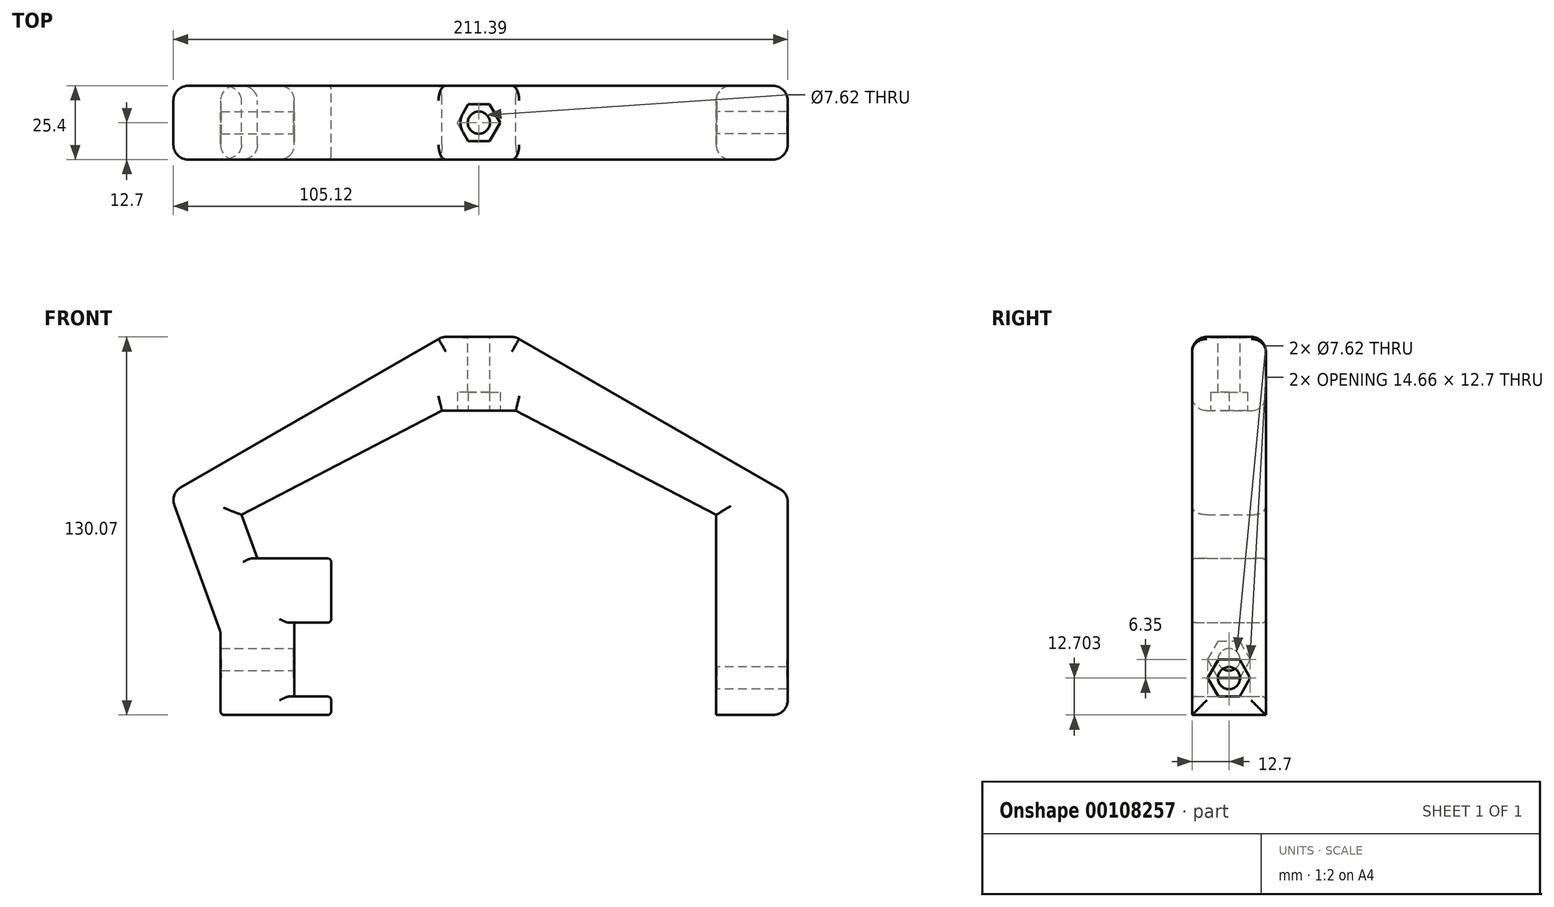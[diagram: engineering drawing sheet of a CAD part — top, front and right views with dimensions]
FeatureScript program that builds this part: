
annotation { "Feature Type Name" : "Feature", "Feature Type Description" : "" }
export const myFeature = defineFeature(function(context is Context, id is Id, definition is map)
    precondition{}
    {
        {
            assignVariable(context, id + "F0", {"name" : "NutDepth", "anyValue" : .25});
        }
        {
            var Q0;
            Q0=qCreatedBy(makeId("Front.planeOp"),FACE);
            var sketch = newSketch(context, id + "F1", { "sketchPlane" : qUnion([Q0])});
            skLineSegment(sketch, "E0", {"start": v(-63.5, 12.08) * mm, "end": v(-63.5, -13.32) * mm});
            skLineSegment(sketch, "E1", {"start": v(-63.5, -13.32) * mm, "end": v(-88.9, -13.32) * mm});
            skLineSegment(sketch, "E2", {"start": v(-63.5, 12.08) * mm, "end": v(-76.2, 12.08) * mm});
            skPoint(sketch, "E3", {"position": v(0, 62.88) * mm});
            skLineSegment(sketch, "E4", {"start": v(-88.9, -13.32) * mm, "end": v(-106.27, 34.41) * mm});
            skLineSegment(sketch, "E5", {"start": v(-76.2, 12.08) * mm, "end": v(-81.66, 27.07) * mm});
            skLineSegment(sketch, "E6", {"start": v(0, 62.88) * mm, "end": v(-12.7, 62.88) * mm});
            skLineSegment(sketch, "E7", {"start": v(0, 88.28) * mm, "end": v(-12.7, 88.28) * mm});
            skLineSegment(sketch, "E8", {"start": v(-81.66, 27.07) * mm, "end": v(-12.7, 62.88) * mm});
            skLineSegment(sketch, "E9", {"start": v(-106.27, 34.41) * mm, "end": v(-12.7, 88.28) * mm});
            skLineSegment(sketch, "E10.MirrorCS", {"start": v(0, 88.28) * mm, "end": v(12.7, 88.28) * mm});
            skLineSegment(sketch, "E11.MirrorCS", {"start": v(106.27, 34.41) * mm, "end": v(12.7, 88.28) * mm});
            skLineSegment(sketch, "E12.MirrorCS", {"start": v(0, 62.88) * mm, "end": v(12.7, 62.88) * mm});
            skLineSegment(sketch, "E13.MirrorCS", {"start": v(81.66, 27.07) * mm, "end": v(12.7, 62.88) * mm});
            skLineSegment(sketch, "E14", {"start": v(81.66, -41.79) * mm, "end": v(106.27, -41.79) * mm});
            skLineSegment(sketch, "E15", {"start": v(106.27, -41.79) * mm, "end": v(106.27, 34.41) * mm});
            skLineSegment(sketch, "E16", {"start": v(81.66, 27.07) * mm, "end": v(81.66, -41.79) * mm});
            skLineSegment(sketch, "E17", {"start": v(-106.27, 34.41) * mm, "end": v(-81.66, 27.07) * mm});
            skLineSegment(sketch, "E18", {"start": v(81.66, 27.07) * mm, "end": v(106.27, 34.41) * mm});
            skSolve(sketch);
        }
        {
            var Q0;
            Q0 = qSketchRegion(id + "F1", true);
            extrude(context, id + "F2", {"entities" : qUnion([Q0]), "endBound" : BoundingType.SYMMETRIC, "depth" : 25.4 * mm});
        }
        {
            var Q0;
            Q0=makeQuery(id+"F2.opExtrude","SWEPT_FACE",FACE,{"disambiguationData":[OSD([sQuery(id+"F1.wireOp",EDGE,"E1")])]});
            var Q1;
            Q1=makeQuery(id+"F2.opExtrude","SWEPT_FACE",FACE,{"disambiguationData":[OSD([sQuery(id+"F1.wireOp",EDGE,"E14")])]});
            extrude(context, id + "F3", {"entities" : qUnion([Q0]), "operationType" : NewBodyOperationType.ADD, "endBound" : BoundingType.UP_TO_SURFACE, "endBoundEntityFace" : qUnion([Q1]), "depth" : 25.4 * mm});
        }
        {
            var Q0;
            Q0=makeQuery(id+"F2.opExtrude","SWEPT_FACE",FACE,{"disambiguationData":[OSD([sQuery(id+"F1.wireOp",EDGE,"E16")])]});
            var sketch = newSketch(context, id + "F4", { "sketchPlane" : qUnion([Q0])});
            skLineSegment(sketch, "E19.0.1", {"start": v(-12.7, -41.79) * mm, "end": v(12.7, -41.79) * mm});
            skCircle(sketch, "E20", {"center": v(0, -29.09) * mm, "radius": 3.81 * mm});
            skCircle(sketch, "E21", {"center": v(0, -29.09) * mm, "radius": 6.35 * mm});
            skCircle(sketch, "E22.cCircle", {"center": v(0, -29.09) * mm, "radius": 6.35 * mm, "construction": true});
            skLineSegment(sketch, "E22.0", {"start": v(-3.67, -35.44) * mm, "end": v(-7.33, -29.09) * mm});
            skLineSegment(sketch, "E22.1", {"start": v(-7.33, -29.09) * mm, "end": v(-3.67, -22.74) * mm});
            skLineSegment(sketch, "E22.2", {"start": v(-3.67, -22.74) * mm, "end": v(3.67, -22.74) * mm});
            skLineSegment(sketch, "E22.3", {"start": v(3.67, -22.74) * mm, "end": v(7.33, -29.09) * mm});
            skLineSegment(sketch, "E22.4", {"start": v(7.33, -29.09) * mm, "end": v(3.67, -35.44) * mm});
            skLineSegment(sketch, "E22.5", {"start": v(3.67, -35.44) * mm, "end": v(-3.67, -35.44) * mm});
            skPoint(sketch, "E22.0.midPoint", {"position": v(-5.5, -32.26) * mm});
            skSolve(sketch);
        }
        {
            var Q0;
            {var subQ0=sQuery(id+"F4.wireOp",EDGE,"E22.2");var subQ1=sQuery(id+"F4.wireOp",EDGE,"E21");var subQ2=makeQuery(id+"F4.imprint","INTERSECT",VERTEX,{"derivedFrom":[subQ1,subQ0]});Q0=makeQuery(id+"F4.imprint","IMPRINT",FACE,{"disambiguationData":[TD([[makeQuery(id+"F4.imprint","IMPRINT",EDGE,{"disambiguationData":[TD([[subQ2,-1.0]])],"derivedFrom":subQ1}),-1.0]])]});}
            var Q1;
            Q1=makeQuery(id+"F4.imprint","IMPRINT",FACE,{"disambiguationData":[TD([[makeQuery(id+"F4.imprint","IMPRINT",EDGE,{"derivedFrom":sQuery(id+"F4.wireOp",EDGE,"E20")}),-1.0]])]});
            var Q2;
            {var subQ0=sQuery(id+"F4.wireOp",EDGE,"E22.1");var subQ1=sQuery(id+"F4.wireOp",EDGE,"E21");var subQ2=makeQuery(id+"F4.imprint","INTERSECT",VERTEX,{"derivedFrom":[subQ1,subQ0]});Q2=makeQuery(id+"F4.imprint","IMPRINT",FACE,{"disambiguationData":[TD([[makeQuery(id+"F4.imprint","IMPRINT",EDGE,{"disambiguationData":[TD([[subQ2,-1.0]])],"derivedFrom":subQ1}),-1.0]])]});}
            var Q3;
            {var subQ0=sQuery(id+"F4.wireOp",EDGE,"E22.2");var subQ1=sQuery(id+"F4.wireOp",EDGE,"E21");var subQ2=makeQuery(id+"F4.imprint","INTERSECT",VERTEX,{"derivedFrom":[subQ1,subQ0]});Q3=makeQuery(id+"F4.imprint","IMPRINT",FACE,{"disambiguationData":[TD([[makeQuery(id+"F4.imprint","IMPRINT",EDGE,{"disambiguationData":[TD([[subQ2,1.0]])],"derivedFrom":subQ1}),-1.0]])]});}
            var Q4;
            {var subQ0=sQuery(id+"F4.wireOp",EDGE,"E22.3");var subQ1=sQuery(id+"F4.wireOp",EDGE,"E21");var subQ2=makeQuery(id+"F4.imprint","INTERSECT",VERTEX,{"derivedFrom":[subQ1,subQ0]});Q4=makeQuery(id+"F4.imprint","IMPRINT",FACE,{"disambiguationData":[TD([[makeQuery(id+"F4.imprint","IMPRINT",EDGE,{"disambiguationData":[TD([[subQ2,1.0]])],"derivedFrom":subQ1}),-1.0]])]});}
            var Q5;
            {var subQ0=sQuery(id+"F4.wireOp",EDGE,"E22.5");var subQ1=sQuery(id+"F4.wireOp",EDGE,"E21");var subQ2=makeQuery(id+"F4.imprint","INTERSECT",VERTEX,{"derivedFrom":[subQ1,subQ0]});Q5=makeQuery(id+"F4.imprint","IMPRINT",FACE,{"disambiguationData":[TD([[makeQuery(id+"F4.imprint","IMPRINT",EDGE,{"disambiguationData":[TD([[subQ2,-1.0]])],"derivedFrom":subQ1}),-1.0]])]});}
            var Q6;
            {var subQ0=sQuery(id+"F4.wireOp",EDGE,"E22.0");var subQ1=sQuery(id+"F4.wireOp",EDGE,"E21");var subQ2=makeQuery(id+"F4.imprint","INTERSECT",VERTEX,{"derivedFrom":[subQ1,subQ0]});Q6=makeQuery(id+"F4.imprint","IMPRINT",FACE,{"disambiguationData":[TD([[makeQuery(id+"F4.imprint","IMPRINT",EDGE,{"disambiguationData":[TD([[subQ2,-1.0]])],"derivedFrom":subQ1}),-1.0]])]});}
            extrude(context, id + "F5", {"entities" : qUnion([Q0, Q1, Q2, Q3, Q4, Q5, Q6]), "operationType" : NewBodyOperationType.REMOVE, "oppositeDirection" : true, "depth" : (getVariable(context, 'NutDepth')) * mm});
        }
        {
            var Q0;
            Q0=makeQuery(id+"F5.boolean.opBoolean","SPLIT",FACE,{"disambiguationData":[TD([makeQuery(id+"F5.opExtrude","SWEPT_FACE",FACE,{"disambiguationData":[OSD([sQuery(id+"F4.wireOp",EDGE,"E20")])]})])],"derivedFrom":makeQuery(id+"F2.opExtrude","SWEPT_FACE",FACE,{"disambiguationData":[OSD([sQuery(id+"F1.wireOp",EDGE,"E16")])]})});
            extrude(context, id + "F6", {"entities" : qUnion([Q0]), "operationType" : NewBodyOperationType.REMOVE, "endBound" : BoundingType.THROUGH_ALL, "oppositeDirection" : true, "depth" : 25.4 * mm});
        }
        {
            var Q0;
            Q0=makeQuery(id+"F2.opExtrude","SWEPT_FACE",FACE,{"disambiguationData":[OSD([sQuery(id+"F1.wireOp",EDGE,"E15")])]});
            var sketch = newSketch(context, id + "F7", { "sketchPlane" : qUnion([Q0])});
            skLineSegment(sketch, "E23.0", {"start": v(3.67, -22.74) * mm, "end": v(-3.67, -22.74) * mm});
            skLineSegment(sketch, "E24.0", {"start": v(-3.67, -22.74) * mm, "end": v(-7.33, -29.09) * mm});
            skLineSegment(sketch, "E25.0", {"start": v(-7.33, -29.09) * mm, "end": v(-3.67, -35.44) * mm});
            skLineSegment(sketch, "E26.0", {"start": v(-3.67, -35.44) * mm, "end": v(3.67, -35.44) * mm});
            skLineSegment(sketch, "E27.0", {"start": v(3.67, -35.44) * mm, "end": v(7.33, -29.09) * mm});
            skLineSegment(sketch, "E28.0", {"start": v(7.33, -29.09) * mm, "end": v(3.67, -22.74) * mm});
            skSolve(sketch);
        }
        {
            var Q0;
            Q0=makeQuery(id+"F7.imprint","IMPRINT",FACE,{"disambiguationData":[TD([[makeQuery(id+"F7.imprint","IMPRINT",EDGE,{"derivedFrom":sQuery(id+"F7.wireOp",EDGE,"E23.0")}),1.0]])]});
            extrude(context, id + "F8", {"entities" : qUnion([Q0]), "operationType" : NewBodyOperationType.REMOVE, "oppositeDirection" : true, "depth" : (getVariable(context, 'NutDepth')) * mm});
        }
        {
            var Q0;
            Q0=makeQuery(id+"F2.opExtrude","SWEPT_FACE",FACE,{"disambiguationData":[OSD([sQuery(id+"F1.wireOp",EDGE,"E7"),sQuery(id+"F1.wireOp",EDGE,"E10.MirrorCS")])]});
            var sketch = newSketch(context, id + "F9", { "sketchPlane" : qUnion([Q0])});
            skLineSegment(sketch, "E29.0.0", {"start": v(12.7, 12.7) * mm, "end": v(-12.7, 12.7) * mm});
            skLineSegment(sketch, "E29.0.1", {"start": v(-12.7, 12.7) * mm, "end": v(-12.7, -12.7) * mm});
            skLineSegment(sketch, "E29.0.2", {"start": v(-12.7, -12.7) * mm, "end": v(12.7, -12.7) * mm});
            skLineSegment(sketch, "E29.0.3", {"start": v(12.7, -12.7) * mm, "end": v(12.7, 12.7) * mm});
            skCircle(sketch, "E30", {"center": v(0, 0) * mm, "radius": 3.81 * mm});
            skCircle(sketch, "E31", {"center": v(0, 0) * mm, "radius": 6.35 * mm});
            skCircle(sketch, "E32.cCircle", {"center": v(0, 0) * mm, "radius": 6.35 * mm, "construction": true});
            skLineSegment(sketch, "E32.0", {"start": v(7.33, 0) * mm, "end": v(3.67, -6.35) * mm});
            skLineSegment(sketch, "E32.1", {"start": v(3.67, -6.35) * mm, "end": v(-3.67, -6.35) * mm});
            skLineSegment(sketch, "E32.2", {"start": v(-3.67, -6.35) * mm, "end": v(-7.33, 0) * mm});
            skLineSegment(sketch, "E32.3", {"start": v(-7.33, 0) * mm, "end": v(-3.67, 6.35) * mm});
            skLineSegment(sketch, "E32.4", {"start": v(-3.67, 6.35) * mm, "end": v(3.67, 6.35) * mm});
            skLineSegment(sketch, "E32.5", {"start": v(3.67, 6.35) * mm, "end": v(7.33, 0) * mm});
            skPoint(sketch, "E32.0.midPoint", {"position": v(5.5, -3.18) * mm});
            skSolve(sketch);
        }
        {
            var Q0;
            {var subQ0=sQuery(id+"F9.wireOp",EDGE,"E32.4");var subQ1=sQuery(id+"F9.wireOp",EDGE,"E31");var subQ2=makeQuery(id+"F9.imprint","INTERSECT",VERTEX,{"derivedFrom":[subQ1,subQ0]});Q0=makeQuery(id+"F9.imprint","IMPRINT",FACE,{"disambiguationData":[TD([[makeQuery(id+"F9.imprint","IMPRINT",EDGE,{"disambiguationData":[TD([[subQ2,-1.0]])],"derivedFrom":subQ1}),-1.0]])]});}
            var Q1;
            {var subQ0=sQuery(id+"F9.wireOp",EDGE,"E32.4");var subQ1=sQuery(id+"F9.wireOp",EDGE,"E31");var subQ2=makeQuery(id+"F9.imprint","INTERSECT",VERTEX,{"derivedFrom":[subQ1,subQ0]});Q1=makeQuery(id+"F9.imprint","IMPRINT",FACE,{"disambiguationData":[TD([[makeQuery(id+"F9.imprint","IMPRINT",EDGE,{"disambiguationData":[TD([[subQ2,1.0]])],"derivedFrom":subQ1}),-1.0]])]});}
            var Q2;
            {var subQ0=sQuery(id+"F9.wireOp",EDGE,"E32.5");var subQ1=sQuery(id+"F9.wireOp",EDGE,"E31");var subQ2=makeQuery(id+"F9.imprint","INTERSECT",VERTEX,{"derivedFrom":[subQ1,subQ0]});Q2=makeQuery(id+"F9.imprint","IMPRINT",FACE,{"disambiguationData":[TD([[makeQuery(id+"F9.imprint","IMPRINT",EDGE,{"disambiguationData":[TD([[subQ2,1.0]])],"derivedFrom":subQ1}),-1.0]])]});}
            var Q3;
            {var subQ0=sQuery(id+"F9.wireOp",EDGE,"E32.1");var subQ1=sQuery(id+"F9.wireOp",EDGE,"E31");var subQ2=makeQuery(id+"F9.imprint","INTERSECT",VERTEX,{"derivedFrom":[subQ1,subQ0]});Q3=makeQuery(id+"F9.imprint","IMPRINT",FACE,{"disambiguationData":[TD([[makeQuery(id+"F9.imprint","IMPRINT",EDGE,{"disambiguationData":[TD([[subQ2,-1.0]])],"derivedFrom":subQ1}),-1.0]])]});}
            var Q4;
            {var subQ0=sQuery(id+"F9.wireOp",EDGE,"E32.2");var subQ1=sQuery(id+"F9.wireOp",EDGE,"E31");var subQ2=makeQuery(id+"F9.imprint","INTERSECT",VERTEX,{"derivedFrom":[subQ1,subQ0]});Q4=makeQuery(id+"F9.imprint","IMPRINT",FACE,{"disambiguationData":[TD([[makeQuery(id+"F9.imprint","IMPRINT",EDGE,{"disambiguationData":[TD([[subQ2,-1.0]])],"derivedFrom":subQ1}),-1.0]])]});}
            var Q5;
            Q5=makeQuery(id+"F9.imprint","IMPRINT",FACE,{"disambiguationData":[TD([[makeQuery(id+"F9.imprint","IMPRINT",EDGE,{"derivedFrom":sQuery(id+"F9.wireOp",EDGE,"E30")}),-1.0]])]});
            extrude(context, id + "F10", {"entities" : qUnion([Q0, Q1, Q2, Q3, Q4, Q5]), "operationType" : NewBodyOperationType.REMOVE, "oppositeDirection" : true, "depth" : (getVariable(context, 'NutDepth')) * mm});
        }
        {
            var Q0;
            Q0=makeQuery(id+"F9.imprint","IMPRINT",FACE,{"disambiguationData":[TD([[makeQuery(id+"F9.imprint","IMPRINT",EDGE,{"derivedFrom":sQuery(id+"F9.wireOp",EDGE,"E30")}),1.0]])]});
            extrude(context, id + "F11", {"entities" : qUnion([Q0]), "operationType" : NewBodyOperationType.REMOVE, "endBound" : BoundingType.THROUGH_ALL, "oppositeDirection" : true, "depth" : 25.4 * mm});
        }
        {
            var Q0;
            Q0=makeQuery(id+"F2.opExtrude","SWEPT_FACE",FACE,{"disambiguationData":[OSD([sQuery(id+"F1.wireOp",EDGE,"E6"),sQuery(id+"F1.wireOp",EDGE,"E12.MirrorCS")])]});
            var sketch = newSketch(context, id + "F12", { "sketchPlane" : qUnion([Q0])});
            skLineSegment(sketch, "E33.0", {"start": v(-3.67, 6.35) * mm, "end": v(-7.33, 0) * mm});
            skLineSegment(sketch, "E34.0", {"start": v(-7.33, 0) * mm, "end": v(-3.67, -6.35) * mm});
            skLineSegment(sketch, "E35.0", {"start": v(-3.67, -6.35) * mm, "end": v(3.67, -6.35) * mm});
            skLineSegment(sketch, "E36.0", {"start": v(3.67, -6.35) * mm, "end": v(7.33, 0) * mm});
            skLineSegment(sketch, "E37.0", {"start": v(7.33, 0) * mm, "end": v(3.67, 6.35) * mm});
            skLineSegment(sketch, "E38.0", {"start": v(3.67, 6.35) * mm, "end": v(-3.67, 6.35) * mm});
            skSolve(sketch);
        }
        {
            var Q0;
            Q0=makeQuery(id+"F12.imprint","IMPRINT",FACE,{"disambiguationData":[TD([[makeQuery(id+"F12.imprint","IMPRINT",EDGE,{"derivedFrom":sQuery(id+"F12.wireOp",EDGE,"E33.0")}),1.0]])]});
            extrude(context, id + "F13", {"entities" : qUnion([Q0]), "operationType" : NewBodyOperationType.REMOVE, "oppositeDirection" : true, "depth" : 6.35 * mm});
        }
        {
            var Q0;
            {var subQ0=sQuery(id+"F1.wireOp",EDGE,"E0");Q0=makeQuery(id+"F3.boolean.opBoolean","MERGE",FACE,{"derivedFrom":[makeQuery(id+"F2.opExtrude","SWEPT_FACE",FACE,{"disambiguationData":[OSD([subQ0])]}),makeQuery(id+"F3.opExtrude","SWEPT_FACE",FACE,{"disambiguationData":[OSD([subQ0,sQuery(id+"F1.wireOp",EDGE,"E1")])]})]});}
            var sketch = newSketch(context, id + "F14", { "sketchPlane" : qUnion([Q0])});
            skLineSegment(sketch, "E39.0.3", {"start": v(-12.7, -41.79) * mm, "end": v(12.7, -41.79) * mm});
            skLineSegment(sketch, "E40.0", {"start": v(-12.7, -16.39) * mm, "end": v(12.7, -16.39) * mm});
            skPoint(sketch, "E41.center.orphan", {"position": v(0, -22.74) * mm});
            skCircle(sketch, "E42", {"center": v(0, -22.74) * mm, "radius": 3.81 * mm});
            skCircle(sketch, "E43", {"center": v(0, -22.74) * mm, "radius": 6.35 * mm});
            skCircle(sketch, "E44.cCircle", {"center": v(0, -22.74) * mm, "radius": 6.35 * mm, "construction": true});
            skLineSegment(sketch, "E44.0", {"start": v(7.33, -22.74) * mm, "end": v(3.67, -29.09) * mm});
            skLineSegment(sketch, "E44.1", {"start": v(3.67, -29.09) * mm, "end": v(-3.67, -29.09) * mm});
            skLineSegment(sketch, "E44.2", {"start": v(-3.67, -29.09) * mm, "end": v(-7.33, -22.74) * mm});
            skLineSegment(sketch, "E44.3", {"start": v(-7.33, -22.74) * mm, "end": v(-3.67, -16.39) * mm});
            skLineSegment(sketch, "E44.4", {"start": v(-3.67, -16.39) * mm, "end": v(3.67, -16.39) * mm});
            skLineSegment(sketch, "E44.5", {"start": v(3.67, -16.39) * mm, "end": v(7.33, -22.74) * mm});
            skPoint(sketch, "E44.0.midPoint", {"position": v(5.5, -25.91) * mm});
            skLineSegment(sketch, "E45.0", {"start": v(-12.7, -10.04) * mm, "end": v(12.7, -10.04) * mm});
            skLineSegment(sketch, "E46.0", {"start": v(-12.7, -35.44) * mm, "end": v(12.7, -35.44) * mm});
            skSolve(sketch);
        }
        {
            var Q0;
            Q0=makeQuery(id+"F14.imprint","IMPRINT",FACE,{"disambiguationData":[TD([[makeQuery(id+"F14.imprint","IMPRINT",EDGE,{"derivedFrom":sQuery(id+"F14.wireOp",EDGE,"E42")}),-1.0]])]});
            var Q1;
            {var subQ0=sQuery(id+"F14.wireOp",EDGE,"E44.4");var subQ1=sQuery(id+"F14.wireOp",EDGE,"E43");var subQ2=makeQuery(id+"F14.imprint","INTERSECT",VERTEX,{"derivedFrom":[subQ1,subQ0]});Q1=makeQuery(id+"F14.imprint","IMPRINT",FACE,{"disambiguationData":[TD([[makeQuery(id+"F14.imprint","IMPRINT",EDGE,{"disambiguationData":[TD([[subQ2,-1.0]])],"derivedFrom":subQ1}),-1.0]])]});}
            var Q2;
            {var subQ0=sQuery(id+"F14.wireOp",EDGE,"E44.3");var subQ1=sQuery(id+"F14.wireOp",EDGE,"E43");var subQ2=makeQuery(id+"F14.imprint","INTERSECT",VERTEX,{"derivedFrom":[subQ1,subQ0]});Q2=makeQuery(id+"F14.imprint","IMPRINT",FACE,{"disambiguationData":[TD([[makeQuery(id+"F14.imprint","IMPRINT",EDGE,{"disambiguationData":[TD([[subQ2,-1.0]])],"derivedFrom":subQ1}),-1.0]])]});}
            var Q3;
            {var subQ0=sQuery(id+"F14.wireOp",EDGE,"E44.2");var subQ1=sQuery(id+"F14.wireOp",EDGE,"E43");var subQ2=makeQuery(id+"F14.imprint","INTERSECT",VERTEX,{"derivedFrom":[subQ1,subQ0]});Q3=makeQuery(id+"F14.imprint","IMPRINT",FACE,{"disambiguationData":[TD([[makeQuery(id+"F14.imprint","IMPRINT",EDGE,{"disambiguationData":[TD([[subQ2,-1.0]])],"derivedFrom":subQ1}),-1.0]])]});}
            var Q4;
            {var subQ0=sQuery(id+"F14.wireOp",EDGE,"E44.1");var subQ1=sQuery(id+"F14.wireOp",EDGE,"E43");var subQ2=makeQuery(id+"F14.imprint","INTERSECT",VERTEX,{"derivedFrom":[subQ1,subQ0]});Q4=makeQuery(id+"F14.imprint","IMPRINT",FACE,{"disambiguationData":[TD([[makeQuery(id+"F14.imprint","IMPRINT",EDGE,{"disambiguationData":[TD([[subQ2,-1.0]])],"derivedFrom":subQ1}),-1.0]])]});}
            var Q5;
            {var subQ0=sQuery(id+"F14.wireOp",EDGE,"E44.5");var subQ1=sQuery(id+"F14.wireOp",EDGE,"E43");var subQ2=makeQuery(id+"F14.imprint","INTERSECT",VERTEX,{"derivedFrom":[subQ1,subQ0]});Q5=makeQuery(id+"F14.imprint","IMPRINT",FACE,{"disambiguationData":[TD([[makeQuery(id+"F14.imprint","IMPRINT",EDGE,{"disambiguationData":[TD([[subQ2,1.0]])],"derivedFrom":subQ1}),-1.0]])]});}
            var Q6;
            {var subQ0=sQuery(id+"F14.wireOp",EDGE,"E44.4");var subQ1=sQuery(id+"F14.wireOp",EDGE,"E43");var subQ2=makeQuery(id+"F14.imprint","INTERSECT",VERTEX,{"derivedFrom":[subQ1,subQ0]});Q6=makeQuery(id+"F14.imprint","IMPRINT",FACE,{"disambiguationData":[TD([[makeQuery(id+"F14.imprint","IMPRINT",EDGE,{"disambiguationData":[TD([[subQ2,1.0]])],"derivedFrom":subQ1}),-1.0]])]});}
            extrude(context, id + "F15", {"entities" : qUnion([Q0, Q1, Q2, Q3, Q4, Q5, Q6]), "operationType" : NewBodyOperationType.REMOVE, "oppositeDirection" : true, "depth" : (getVariable(context, 'NutDepth')) * mm});
        }
        {
            var Q0;
            Q0=makeQuery(id+"F14.imprint","IMPRINT",FACE,{"disambiguationData":[TD([[makeQuery(id+"F14.imprint","IMPRINT",EDGE,{"derivedFrom":sQuery(id+"F14.wireOp",EDGE,"E42")}),1.0]])]});
            extrude(context, id + "F16", {"entities" : qUnion([Q0]), "operationType" : NewBodyOperationType.REMOVE, "endBound" : BoundingType.THROUGH_ALL, "oppositeDirection" : true, "depth" : 25.4 * mm});
        }
        {
            var Q0;
            Q0=makeQuery(id+"F3.opExtrude","SWEPT_FACE",FACE,{"disambiguationData":[OSD([sQuery(id+"F1.wireOp",EDGE,"E1"),sQuery(id+"F1.wireOp",EDGE,"E4")])]});
            var sketch = newSketch(context, id + "F17", { "sketchPlane" : qUnion([Q0])});
            skLineSegment(sketch, "E47.0", {"start": v(3.67, -16.39) * mm, "end": v(-3.67, -16.39) * mm});
            skLineSegment(sketch, "E48.0", {"start": v(-3.67, -16.39) * mm, "end": v(-7.33, -22.74) * mm});
            skLineSegment(sketch, "E49.0", {"start": v(-7.33, -22.74) * mm, "end": v(-3.67, -29.09) * mm});
            skLineSegment(sketch, "E50.0", {"start": v(-3.67, -29.09) * mm, "end": v(3.67, -29.09) * mm});
            skLineSegment(sketch, "E51.0", {"start": v(3.67, -29.09) * mm, "end": v(7.33, -22.74) * mm});
            skLineSegment(sketch, "E52.0", {"start": v(7.33, -22.74) * mm, "end": v(3.67, -16.39) * mm});
            skSolve(sketch);
        }
        {
            var Q0;
            Q0=makeQuery(id+"F17.imprint","IMPRINT",FACE,{"disambiguationData":[TD([[makeQuery(id+"F17.imprint","IMPRINT",EDGE,{"derivedFrom":sQuery(id+"F17.wireOp",EDGE,"E47.0")}),1.0]])]});
            extrude(context, id + "F18", {"entities" : qUnion([Q0]), "operationType" : NewBodyOperationType.REMOVE, "oppositeDirection" : true, "depth" : (getVariable(context, 'NutDepth')) * mm});
        }
        {
            var Q0;
            Q0=makeQuery(id+"F2.opExtrude","CAP_EDGE",EDGE,{"disambiguationData":[OSD([sQuery(id+"F1.wireOp",EDGE,"E9")])],"isStart":false});
            var Q1;
            Q1=makeQuery(id+"F2.opExtrude","CAP_EDGE",EDGE,{"disambiguationData":[OSD([sQuery(id+"F1.wireOp",EDGE,"E11.MirrorCS")])],"isStart":false});
            var Q2;
            Q2=makeQuery(id+"F2.opExtrude","CAP_EDGE",EDGE,{"disambiguationData":[OSD([sQuery(id+"F1.wireOp",EDGE,"E11.MirrorCS")])],"isStart":true});
            var Q3;
            Q3=makeQuery(id+"F2.opExtrude","CAP_EDGE",EDGE,{"disambiguationData":[OSD([sQuery(id+"F1.wireOp",EDGE,"E9")])],"isStart":true});
            var Q4;
            Q4=makeQuery(id+"F2.opExtrude","CAP_EDGE",EDGE,{"disambiguationData":[OSD([sQuery(id+"F1.wireOp",EDGE,"E15")])],"isStart":false});
            var Q5;
            Q5=makeQuery(id+"F2.opExtrude","CAP_EDGE",EDGE,{"disambiguationData":[OSD([sQuery(id+"F1.wireOp",EDGE,"E15")])],"isStart":true});
            var Q6;
            Q6=makeQuery(id+"F2.opExtrude","SWEPT_EDGE",EDGE,{"disambiguationData":[OSD([sQuery(id+"F1.wireOp",EDGE,"E11.MirrorCS"),sQuery(id+"F1.wireOp",EDGE,"E15"),sQuery(id+"F1.wireOp",EDGE,"E18")])]});
            var Q7;
            Q7=makeQuery(id+"F2.opExtrude","CAP_EDGE",EDGE,{"disambiguationData":[OSD([sQuery(id+"F1.wireOp",EDGE,"E16")])],"isStart":false});
            var Q8;
            Q8=makeQuery(id+"F2.opExtrude","CAP_EDGE",EDGE,{"disambiguationData":[OSD([sQuery(id+"F1.wireOp",EDGE,"E16")])],"isStart":true});
            var Q9;
            Q9=makeQuery(id+"F2.opExtrude","CAP_EDGE",EDGE,{"disambiguationData":[OSD([sQuery(id+"F1.wireOp",EDGE,"E13.MirrorCS")])],"isStart":true});
            var Q10;
            Q10=makeQuery(id+"F2.opExtrude","CAP_EDGE",EDGE,{"disambiguationData":[OSD([sQuery(id+"F1.wireOp",EDGE,"E13.MirrorCS")])],"isStart":false});
            var Q11;
            Q11=makeQuery(id+"F2.opExtrude","CAP_EDGE",EDGE,{"disambiguationData":[OSD([sQuery(id+"F1.wireOp",EDGE,"E6"),sQuery(id+"F1.wireOp",EDGE,"E12.MirrorCS")])],"isStart":true});
            var Q12;
            Q12=makeQuery(id+"F2.opExtrude","CAP_EDGE",EDGE,{"disambiguationData":[OSD([sQuery(id+"F1.wireOp",EDGE,"E6"),sQuery(id+"F1.wireOp",EDGE,"E12.MirrorCS")])],"isStart":false});
            var Q13;
            Q13=makeQuery(id+"F2.opExtrude","CAP_EDGE",EDGE,{"disambiguationData":[OSD([sQuery(id+"F1.wireOp",EDGE,"E8")])],"isStart":false});
            var Q14;
            Q14=makeQuery(id+"F2.opExtrude","CAP_EDGE",EDGE,{"disambiguationData":[OSD([sQuery(id+"F1.wireOp",EDGE,"E8")])],"isStart":true});
            var Q15;
            Q15=makeQuery(id+"F2.opExtrude","CAP_EDGE",EDGE,{"disambiguationData":[OSD([sQuery(id+"F1.wireOp",EDGE,"E5")])],"isStart":true});
            var Q16;
            Q16=makeQuery(id+"F2.opExtrude","CAP_EDGE",EDGE,{"disambiguationData":[OSD([sQuery(id+"F1.wireOp",EDGE,"E5")])],"isStart":false});
            var Q17;
            Q17=makeQuery(id+"F2.opExtrude","CAP_EDGE",EDGE,{"disambiguationData":[OSD([sQuery(id+"F1.wireOp",EDGE,"E4")])],"isStart":true});
            var Q18;
            Q18=makeQuery(id+"F2.opExtrude","CAP_EDGE",EDGE,{"disambiguationData":[OSD([sQuery(id+"F1.wireOp",EDGE,"E4")])],"isStart":false});
            var Q19;
            {var subQ0=sQuery(id+"F1.wireOp",EDGE,"E4");var subQ1=sQuery(id+"F1.wireOp",EDGE,"E1");Q19=makeQuery(id+"F3.opExtrude","SWEPT_EDGE",EDGE,{"disambiguationData":[OSD([subQ1,subQ0]),TDD([makeQuery(id+"F2.opExtrude","CAP_VERTEX",VERTEX,{"disambiguationData":[OSD([subQ1,subQ0])],"isStart":false})])]});}
            var Q20;
            {var subQ0=sQuery(id+"F1.wireOp",EDGE,"E4");var subQ1=sQuery(id+"F1.wireOp",EDGE,"E1");Q20=makeQuery(id+"F3.opExtrude","SWEPT_EDGE",EDGE,{"disambiguationData":[OSD([subQ1,subQ0]),TDD([makeQuery(id+"F2.opExtrude","CAP_VERTEX",VERTEX,{"disambiguationData":[OSD([subQ1,subQ0])],"isStart":true})])]});}
            var Q21;
            Q21=makeQuery(id+"F2.opExtrude","SWEPT_EDGE",EDGE,{"disambiguationData":[OSD([sQuery(id+"F1.wireOp",EDGE,"E4"),sQuery(id+"F1.wireOp",EDGE,"E9"),sQuery(id+"F1.wireOp",EDGE,"E17")])]});
            var Q22;
            {var subQ0=sQuery(id+"F1.wireOp",EDGE,"E4");var subQ1=sQuery(id+"F1.wireOp",EDGE,"E1");Q22=makeQuery(id+"F3.boolean.opBoolean","MERGE",EDGE,{"derivedFrom":[makeQuery(id+"F2.opExtrude","SWEPT_EDGE",EDGE,{"disambiguationData":[OSD([subQ1,subQ0])]}),makeQuery(id+"F3.opExtrude","CAP_EDGE",EDGE,{"disambiguationData":[OSD([subQ1,subQ0])],"isStart":true})]});}
            var Q23;
            Q23=makeQuery(id+"F3.opExtrude","TWEAK_EDGE",EDGE,{"derivedFrom":[makeQuery(id+"F2.opExtrude","SWEPT_EDGE",EDGE,{"disambiguationData":[OSD([sQuery(id+"F1.wireOp",EDGE,"E1"),sQuery(id+"F1.wireOp",EDGE,"E4")])]}),makeQuery(id+"F2.opExtrude","SWEPT_FACE",FACE,{"disambiguationData":[OSD([sQuery(id+"F1.wireOp",EDGE,"E14")])]})]});
            var Q24;
            Q24=makeQuery(id+"F2.opExtrude","SWEPT_EDGE",EDGE,{"disambiguationData":[OSD([sQuery(id+"F1.wireOp",EDGE,"E14"),sQuery(id+"F1.wireOp",EDGE,"E15")])]});
            fillet(context, id + "F19", {"entities" : qUnion([Q0, Q1, Q2, Q3, Q4, Q5, Q6, Q7, Q8, Q9, Q10, Q11, Q12, Q13, Q14, Q15, Q16, Q17, Q18, Q19, Q20, Q21, Q22, Q23, Q24]), "radius" : 5.08 * mm, "tangentPropagation" : true, "allowEdgeOverflow" : false});
        }
        {
            var Q0;
            Q0=makeQuery(id+"F2.opExtrude","CAP_EDGE",EDGE,{"disambiguationData":[OSD([sQuery(id+"F1.wireOp",EDGE,"E7"),sQuery(id+"F1.wireOp",EDGE,"E10.MirrorCS")])],"isStart":true});
            fillet(context, id + "F20", {"entities" : qUnion([Q0]), "radius" : 5.08 * mm, "tangentPropagation" : true, "allowEdgeOverflow" : false});
        }
        {
            var Q0;
            {var subQ0=sQuery(id+"F14.wireOp",EDGE,"E45.0");Q0=makeQuery(id+"F14.imprint","IMPRINT",FACE,{"disambiguationData":[TD([[makeQuery(id+"F14.imprint","IMPRINT",EDGE,{"derivedFrom":subQ0}),1.0]])]});}
            extrude(context, id + "F21", {"entities" : qUnion([Q0]), "operationType" : NewBodyOperationType.ADD, "depth" : 12.7 * mm});
        }
        {
            var Q0;
            {var subQ0=sQuery(id+"F14.wireOp",EDGE,"E39.0.3");Q0=makeQuery(id+"F14.imprint","IMPRINT",FACE,{"disambiguationData":[TD([[makeQuery(id+"F14.imprint","IMPRINT",EDGE,{"derivedFrom":subQ0}),-1.0]])]});}
            var Q1;
            Q1=makeQuery(id+"F21.opExtrude","CAP_FACE",FACE,{"disambiguationData":[OSD([sQuery(id+"F1.wireOp",EDGE,"E0"),sQuery(id+"F1.wireOp",EDGE,"E1"),sQuery(id+"F1.wireOp",EDGE,"E2"),sQuery(id+"F14.wireOp",EDGE,"E45.0")])],"isStart":false});
            extrude(context, id + "F22", {"entities" : qUnion([Q0]), "operationType" : NewBodyOperationType.ADD, "endBound" : BoundingType.UP_TO_SURFACE, "endBoundEntityFace" : qUnion([Q1]), "depth" : 25.4 * mm});
        }
        {
            var Q0;
            {var subQ0=sQuery(id+"F1.wireOp",EDGE,"E1");var subQ1=sQuery(id+"F1.wireOp",EDGE,"E0");Q0=makeQuery(id+"F3.boolean.opBoolean","MERGE",EDGE,{"derivedFrom":[makeQuery(id+"F2.opExtrude","CAP_EDGE",EDGE,{"disambiguationData":[OSD([subQ1])],"isStart":false}),makeQuery(id+"F3.opExtrude","SWEPT_EDGE",EDGE,{"disambiguationData":[OSD([subQ1,subQ0]),TDD([makeQuery(id+"F2.opExtrude","CAP_VERTEX",VERTEX,{"disambiguationData":[OSD([subQ1,subQ0])],"isStart":false})])]})]});}
            var Q1;
            {var subQ0=sQuery(id+"F1.wireOp",EDGE,"E1");var subQ1=sQuery(id+"F1.wireOp",EDGE,"E0");Q1=makeQuery(id+"F3.boolean.opBoolean","MERGE",EDGE,{"derivedFrom":[makeQuery(id+"F2.opExtrude","CAP_EDGE",EDGE,{"disambiguationData":[OSD([subQ1])],"isStart":true}),makeQuery(id+"F3.opExtrude","SWEPT_EDGE",EDGE,{"disambiguationData":[OSD([subQ1,subQ0]),TDD([makeQuery(id+"F2.opExtrude","CAP_VERTEX",VERTEX,{"disambiguationData":[OSD([subQ1,subQ0])],"isStart":true})])]})]});}
            fillet(context, id + "F23", {"entities" : qUnion([Q0, Q1]), "radius" : 5.08 * mm, "tangentPropagation" : true, "allowEdgeOverflow" : false});
        }
        {
            var Q0;
            {var subQ0=sQuery(id+"F1.wireOp",EDGE,"E1");var subQ1=sQuery(id+"F1.wireOp",EDGE,"E0");var subQ2=makeQuery(id+"F3.boolean.opBoolean","MERGE",EDGE,{"derivedFrom":[makeQuery(id+"F2.opExtrude","CAP_EDGE",EDGE,{"disambiguationData":[OSD([subQ1])],"isStart":false}),makeQuery(id+"F3.opExtrude","SWEPT_EDGE",EDGE,{"disambiguationData":[OSD([subQ1,subQ0]),TDD([makeQuery(id+"F2.opExtrude","CAP_VERTEX",VERTEX,{"disambiguationData":[OSD([subQ1,subQ0])],"isStart":false})])]})]});Q0=makeQuery(id+"F21.opExtrude","CAP_EDGE",EDGE,{"disambiguationData":[OSD([subQ1,subQ0]),TDD([makeQuery(id+"F14.imprint","IMPRINT",EDGE,{"disambiguationData":[TD([[makeQuery(id+"F14.imprint","INTERSECT",VERTEX,{"derivedFrom":[subQ2,sQuery(id+"F14.wireOp",EDGE,"E45.0")]}),1.0]])],"derivedFrom":subQ2})])],"isStart":false});}
            var Q1;
            Q1=makeQuery(id+"F21.opExtrude","CAP_EDGE",EDGE,{"disambiguationData":[OSD([sQuery(id+"F1.wireOp",EDGE,"E0"),sQuery(id+"F1.wireOp",EDGE,"E2")])],"isStart":false});
            var Q2;
            {var subQ0=sQuery(id+"F1.wireOp",EDGE,"E1");var subQ1=sQuery(id+"F1.wireOp",EDGE,"E0");var subQ2=makeQuery(id+"F3.boolean.opBoolean","MERGE",EDGE,{"derivedFrom":[makeQuery(id+"F2.opExtrude","CAP_EDGE",EDGE,{"disambiguationData":[OSD([subQ1])],"isStart":true}),makeQuery(id+"F3.opExtrude","SWEPT_EDGE",EDGE,{"disambiguationData":[OSD([subQ1,subQ0]),TDD([makeQuery(id+"F2.opExtrude","CAP_VERTEX",VERTEX,{"disambiguationData":[OSD([subQ1,subQ0])],"isStart":true})])]})]});Q2=makeQuery(id+"F21.opExtrude","CAP_EDGE",EDGE,{"disambiguationData":[OSD([subQ1,subQ0]),TDD([makeQuery(id+"F14.imprint","IMPRINT",EDGE,{"disambiguationData":[TD([[makeQuery(id+"F14.imprint","INTERSECT",VERTEX,{"derivedFrom":[subQ2,sQuery(id+"F14.wireOp",EDGE,"E45.0")]}),1.0]])],"derivedFrom":subQ2})])],"isStart":false});}
            var Q3;
            Q3=makeQuery(id+"F21.opExtrude","CAP_EDGE",EDGE,{"disambiguationData":[OSD([sQuery(id+"F14.wireOp",EDGE,"E45.0")])],"isStart":false});
            var Q4;
            Q4=makeQuery(id+"F22.opExtrude","CAP_FACE",FACE,{"disambiguationData":[OSD([sQuery(id+"F1.wireOp",EDGE,"E0"),sQuery(id+"F1.wireOp",EDGE,"E1"),sQuery(id+"F1.wireOp",EDGE,"E2"),sQuery(id+"F14.wireOp",EDGE,"E45.0")])],"isStart":false});
            var Q5;
            {var subQ0=sQuery(id+"F1.wireOp",EDGE,"E1");var subQ1=sQuery(id+"F1.wireOp",EDGE,"E0");var subQ2=sQuery(id+"F1.wireOp",EDGE,"E2");Q5=makeQuery(id+"F21.boolean.opBoolean","MERGE",EDGE,{"derivedFrom":[makeQuery(id+"F2.opExtrude","CAP_EDGE",EDGE,{"disambiguationData":[OSD([subQ2])],"isStart":false}),makeQuery(id+"F21.opExtrude","SWEPT_EDGE",EDGE,{"disambiguationData":[OSD([subQ1,subQ0,subQ2]),TDD([makeQuery(id+"F14.imprint","INTERSECT",VERTEX,{"derivedFrom":[makeQuery(id+"F2.opExtrude","SWEPT_EDGE",EDGE,{"disambiguationData":[OSD([subQ1,subQ2])]}),makeQuery(id+"F3.boolean.opBoolean","MERGE",EDGE,{"derivedFrom":[makeQuery(id+"F2.opExtrude","CAP_EDGE",EDGE,{"disambiguationData":[OSD([subQ1])],"isStart":false}),makeQuery(id+"F3.opExtrude","SWEPT_EDGE",EDGE,{"disambiguationData":[OSD([subQ1,subQ0]),TDD([makeQuery(id+"F2.opExtrude","CAP_VERTEX",VERTEX,{"disambiguationData":[OSD([subQ1,subQ0])],"isStart":false})])]})]})]})])]})]});}
            var Q6;
            {var subQ0=sQuery(id+"F14.wireOp",EDGE,"E45.0");var subQ1=sQuery(id+"F1.wireOp",EDGE,"E1");var subQ2=sQuery(id+"F1.wireOp",EDGE,"E0");Q6=makeQuery(id+"F21.opExtrude","SWEPT_EDGE",EDGE,{"disambiguationData":[OSD([subQ2,subQ1,subQ0]),TDD([makeQuery(id+"F14.imprint","INTERSECT",VERTEX,{"derivedFrom":[makeQuery(id+"F3.boolean.opBoolean","MERGE",EDGE,{"derivedFrom":[makeQuery(id+"F2.opExtrude","CAP_EDGE",EDGE,{"disambiguationData":[OSD([subQ2])],"isStart":false}),makeQuery(id+"F3.opExtrude","SWEPT_EDGE",EDGE,{"disambiguationData":[OSD([subQ2,subQ1]),TDD([makeQuery(id+"F2.opExtrude","CAP_VERTEX",VERTEX,{"disambiguationData":[OSD([subQ2,subQ1])],"isStart":false})])]})]}),subQ0]})])]});}
            var Q7;
            {var subQ0=sQuery(id+"F14.wireOp",EDGE,"E46.0");var subQ1=sQuery(id+"F1.wireOp",EDGE,"E1");var subQ2=sQuery(id+"F1.wireOp",EDGE,"E0");Q7=makeQuery(id+"F22.opExtrude","SWEPT_EDGE",EDGE,{"disambiguationData":[OSD([subQ2,subQ1,subQ0]),TDD([makeQuery(id+"F14.imprint","INTERSECT",VERTEX,{"derivedFrom":[makeQuery(id+"F3.boolean.opBoolean","MERGE",EDGE,{"derivedFrom":[makeQuery(id+"F2.opExtrude","CAP_EDGE",EDGE,{"disambiguationData":[OSD([subQ2])],"isStart":false}),makeQuery(id+"F3.opExtrude","SWEPT_EDGE",EDGE,{"disambiguationData":[OSD([subQ2,subQ1]),TDD([makeQuery(id+"F2.opExtrude","CAP_VERTEX",VERTEX,{"disambiguationData":[OSD([subQ2,subQ1])],"isStart":false})])]})]}),subQ0]})])]});}
            var Q8;
            {var subQ0=sQuery(id+"F14.wireOp",EDGE,"E39.0.3");var subQ1=sQuery(id+"F1.wireOp",EDGE,"E1");var subQ2=sQuery(id+"F1.wireOp",EDGE,"E0");Q8=makeQuery(id+"F22.boolean.opBoolean","MERGE",EDGE,{"derivedFrom":[makeQuery(id+"F3.opExtrude","TWEAK_EDGE",EDGE,{"derivedFrom":[makeQuery(id+"F2.opExtrude","CAP_EDGE",EDGE,{"disambiguationData":[OSD([subQ1])],"isStart":false}),makeQuery(id+"F2.opExtrude","SWEPT_FACE",FACE,{"disambiguationData":[OSD([sQuery(id+"F1.wireOp",EDGE,"E14")])]})]}),makeQuery(id+"F22.opExtrude","SWEPT_EDGE",EDGE,{"disambiguationData":[OSD([subQ2,subQ1,subQ0]),TDD([makeQuery(id+"F14.imprint","INTERSECT",VERTEX,{"derivedFrom":[makeQuery(id+"F3.boolean.opBoolean","MERGE",EDGE,{"derivedFrom":[makeQuery(id+"F2.opExtrude","CAP_EDGE",EDGE,{"disambiguationData":[OSD([subQ2])],"isStart":false}),makeQuery(id+"F3.opExtrude","SWEPT_EDGE",EDGE,{"disambiguationData":[OSD([subQ2,subQ1]),TDD([makeQuery(id+"F2.opExtrude","CAP_VERTEX",VERTEX,{"disambiguationData":[OSD([subQ2,subQ1])],"isStart":false})])]})]}),subQ0]})])]})]});}
            var Q9;
            {var subQ0=sQuery(id+"F1.wireOp",EDGE,"E1");var subQ1=sQuery(id+"F1.wireOp",EDGE,"E0");var subQ2=sQuery(id+"F1.wireOp",EDGE,"E2");Q9=makeQuery(id+"F21.boolean.opBoolean","MERGE",EDGE,{"derivedFrom":[makeQuery(id+"F2.opExtrude","CAP_EDGE",EDGE,{"disambiguationData":[OSD([subQ2])],"isStart":true}),makeQuery(id+"F21.opExtrude","SWEPT_EDGE",EDGE,{"disambiguationData":[OSD([subQ1,subQ0,subQ2]),TDD([makeQuery(id+"F14.imprint","INTERSECT",VERTEX,{"derivedFrom":[makeQuery(id+"F2.opExtrude","SWEPT_EDGE",EDGE,{"disambiguationData":[OSD([subQ1,subQ2])]}),makeQuery(id+"F3.boolean.opBoolean","MERGE",EDGE,{"derivedFrom":[makeQuery(id+"F2.opExtrude","CAP_EDGE",EDGE,{"disambiguationData":[OSD([subQ1])],"isStart":true}),makeQuery(id+"F3.opExtrude","SWEPT_EDGE",EDGE,{"disambiguationData":[OSD([subQ1,subQ0]),TDD([makeQuery(id+"F2.opExtrude","CAP_VERTEX",VERTEX,{"disambiguationData":[OSD([subQ1,subQ0])],"isStart":true})])]})]})]})])]})]});}
            var Q10;
            {var subQ0=sQuery(id+"F14.wireOp",EDGE,"E45.0");var subQ1=sQuery(id+"F1.wireOp",EDGE,"E1");var subQ2=sQuery(id+"F1.wireOp",EDGE,"E0");Q10=makeQuery(id+"F21.opExtrude","SWEPT_EDGE",EDGE,{"disambiguationData":[OSD([subQ2,subQ1,subQ0]),TDD([makeQuery(id+"F14.imprint","INTERSECT",VERTEX,{"derivedFrom":[makeQuery(id+"F3.boolean.opBoolean","MERGE",EDGE,{"derivedFrom":[makeQuery(id+"F2.opExtrude","CAP_EDGE",EDGE,{"disambiguationData":[OSD([subQ2])],"isStart":true}),makeQuery(id+"F3.opExtrude","SWEPT_EDGE",EDGE,{"disambiguationData":[OSD([subQ2,subQ1]),TDD([makeQuery(id+"F2.opExtrude","CAP_VERTEX",VERTEX,{"disambiguationData":[OSD([subQ2,subQ1])],"isStart":true})])]})]}),subQ0]})])]});}
            var Q11;
            {var subQ0=sQuery(id+"F14.wireOp",EDGE,"E46.0");var subQ1=sQuery(id+"F1.wireOp",EDGE,"E1");var subQ2=sQuery(id+"F1.wireOp",EDGE,"E0");Q11=makeQuery(id+"F22.opExtrude","SWEPT_EDGE",EDGE,{"disambiguationData":[OSD([subQ2,subQ1,subQ0]),TDD([makeQuery(id+"F14.imprint","INTERSECT",VERTEX,{"derivedFrom":[makeQuery(id+"F3.boolean.opBoolean","MERGE",EDGE,{"derivedFrom":[makeQuery(id+"F2.opExtrude","CAP_EDGE",EDGE,{"disambiguationData":[OSD([subQ2])],"isStart":true}),makeQuery(id+"F3.opExtrude","SWEPT_EDGE",EDGE,{"disambiguationData":[OSD([subQ2,subQ1]),TDD([makeQuery(id+"F2.opExtrude","CAP_VERTEX",VERTEX,{"disambiguationData":[OSD([subQ2,subQ1])],"isStart":true})])]})]}),subQ0]})])]});}
            var Q12;
            {var subQ0=sQuery(id+"F14.wireOp",EDGE,"E39.0.3");var subQ1=sQuery(id+"F1.wireOp",EDGE,"E1");var subQ2=sQuery(id+"F1.wireOp",EDGE,"E0");Q12=makeQuery(id+"F22.boolean.opBoolean","MERGE",EDGE,{"derivedFrom":[makeQuery(id+"F3.opExtrude","TWEAK_EDGE",EDGE,{"derivedFrom":[makeQuery(id+"F2.opExtrude","CAP_EDGE",EDGE,{"disambiguationData":[OSD([subQ1])],"isStart":true}),makeQuery(id+"F2.opExtrude","SWEPT_FACE",FACE,{"disambiguationData":[OSD([sQuery(id+"F1.wireOp",EDGE,"E14")])]})]}),makeQuery(id+"F22.opExtrude","SWEPT_EDGE",EDGE,{"disambiguationData":[OSD([subQ2,subQ1,subQ0]),TDD([makeQuery(id+"F14.imprint","INTERSECT",VERTEX,{"derivedFrom":[makeQuery(id+"F3.boolean.opBoolean","MERGE",EDGE,{"derivedFrom":[makeQuery(id+"F2.opExtrude","CAP_EDGE",EDGE,{"disambiguationData":[OSD([subQ2])],"isStart":true}),makeQuery(id+"F3.opExtrude","SWEPT_EDGE",EDGE,{"disambiguationData":[OSD([subQ2,subQ1]),TDD([makeQuery(id+"F2.opExtrude","CAP_VERTEX",VERTEX,{"disambiguationData":[OSD([subQ2,subQ1])],"isStart":true})])]})]}),subQ0]})])]})]});}
            fillet(context, id + "F24", {"entities" : qUnion([Q0, Q1, Q2, Q3, Q4, Q5, Q6, Q7, Q8, Q9, Q10, Q11, Q12]), "radius" : 1.27 * mm, "tangentPropagation" : true, "allowEdgeOverflow" : false});
        }
    });
